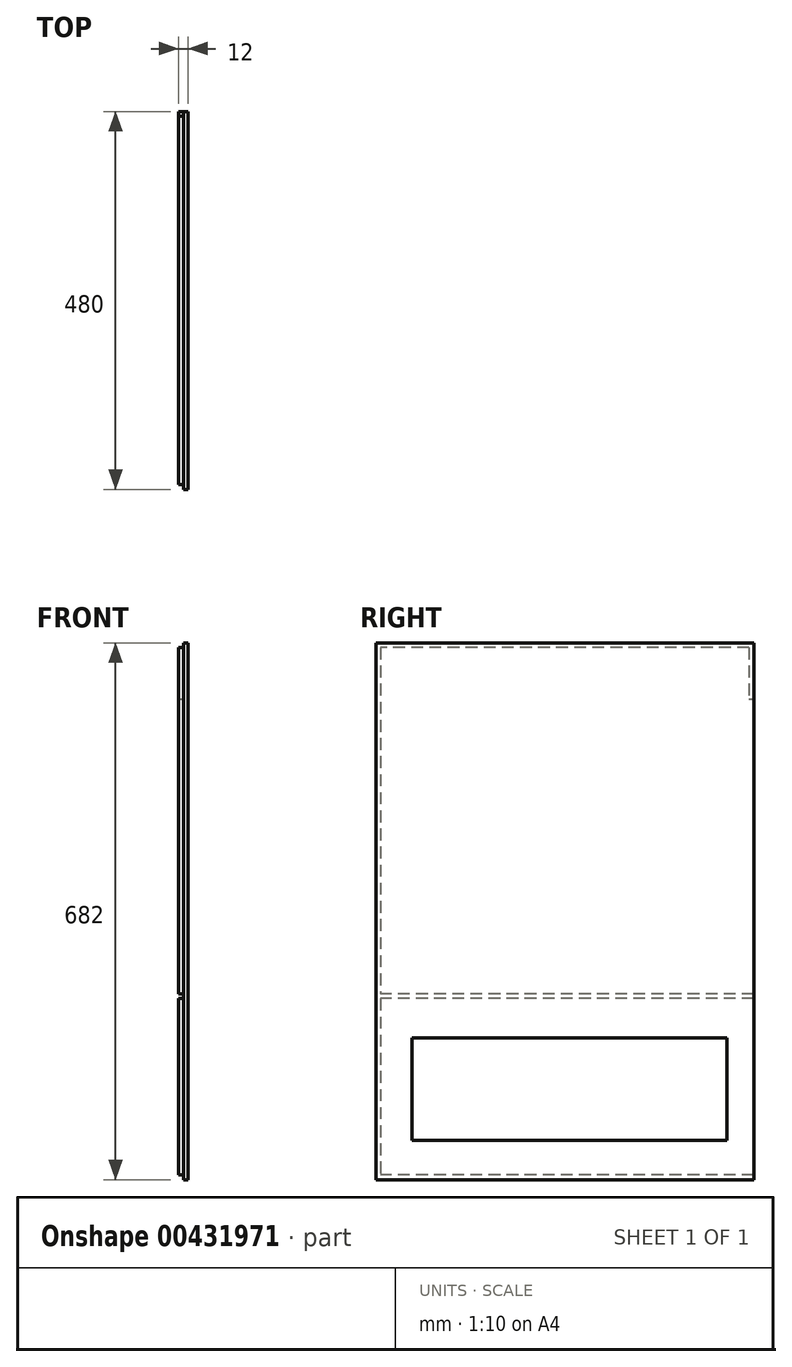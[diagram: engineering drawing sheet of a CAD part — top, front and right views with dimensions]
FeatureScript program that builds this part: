
annotation { "Feature Type Name" : "Feature", "Feature Type Description" : "" }
export const myFeature = defineFeature(function(context is Context, id is Id, definition is map)
    precondition{}
    {
        {
            var Q0;
            Q0=qCreatedBy(makeId("Right.planeOp"),FACE);
            var sketch = newSketch(context, id + "F0", { "sketchPlane" : qUnion([Q0])});
            skLineSegment(sketch, "E0.bottom", {"start": v(-240, 341) * mm, "end": v(240, 341) * mm});
            skLineSegment(sketch, "E0.top", {"start": v(-240, -341) * mm, "end": v(240, -341) * mm});
            skLineSegment(sketch, "E0.left", {"start": v(-240, 341) * mm, "end": v(-240, -341) * mm});
            skLineSegment(sketch, "E0.right", {"start": v(240, 341) * mm, "end": v(240, -341) * mm});
            skPoint(sketch, "E0.middle", {"position": v(0, 0) * mm});
            skSolve(sketch);
        }
        {
            var Q0;
            Q0=makeQuery(id+"F0.imprint","IMPRINT",FACE,{"disambiguationData":[TD([[makeQuery(id+"F0.imprint","IMPRINT",EDGE,{"derivedFrom":sQuery(id+"F0.wireOp",EDGE,"E0.bottom")}),-1.0]])]});
            extrude(context, id + "F1", {"entities" : qUnion([Q0]), "depth" : 12 * mm, "offsetDistance" : 25 * mm});
        }
        {
            var Q0;
            Q0=makeQuery(id+"F1.opExtrude","CAP_FACE",FACE,{"disambiguationData":[OSD([sQuery(id+"F0.wireOp",EDGE,"E0.bottom"),sQuery(id+"F0.wireOp",EDGE,"E0.top"),sQuery(id+"F0.wireOp",EDGE,"E0.left"),sQuery(id+"F0.wireOp",EDGE,"E0.right")])],"isStart":true});
            var sketch = newSketch(context, id + "F2", { "sketchPlane" : qUnion([Q0])});
            skLineSegment(sketch, "E1.bottom", {"start": v(240, 341) * mm, "end": v(234, 341) * mm});
            skLineSegment(sketch, "E1.top", {"start": v(240, -341) * mm, "end": v(234, -341) * mm});
            skLineSegment(sketch, "E1.left", {"start": v(240, 341) * mm, "end": v(240, -341) * mm});
            skLineSegment(sketch, "E1.right", {"start": v(234, 341) * mm, "end": v(234, -341) * mm});
            skSolve(sketch);
        }
        {
            var Q0;
            Q0=qSketchRegion(id+"F2",true);
            extrude(context, id + "F3", {"entities" : qUnion([Q0]), "operationType" : NewBodyOperationType.REMOVE, "oppositeDirection" : true, "depth" : 6 * mm, "offsetDistance" : 25 * mm});
        }
        {
            var Q0;
            {var subQ0=sQuery(id+"F0.wireOp",EDGE,"E0.bottom");var subQ1=sQuery(id+"F0.wireOp",EDGE,"E0.right");var subQ2=sQuery(id+"F0.wireOp",EDGE,"E0.top");Q0=makeQuery(id+"F3.boolean.opBoolean","SPLIT",FACE,{"disambiguationData":[TD([makeQuery(id+"F1.opExtrude","SWEPT_FACE",FACE,{"disambiguationData":[OSD([subQ1])]})])],"derivedFrom":makeQuery(id+"F1.opExtrude","CAP_FACE",FACE,{"disambiguationData":[OSD([subQ0,subQ2,sQuery(id+"F0.wireOp",EDGE,"E0.left"),subQ1])],"isStart":true})});}
            var sketch = newSketch(context, id + "F4", { "sketchPlane" : qUnion([Q0])});
            skLineSegment(sketch, "E2.bottom", {"start": v(-240, 341) * mm, "end": v(234, 341) * mm});
            skLineSegment(sketch, "E2.top", {"start": v(-240, 335) * mm, "end": v(234, 335) * mm});
            skLineSegment(sketch, "E2.left", {"start": v(-240, 341) * mm, "end": v(-240, 335) * mm});
            skLineSegment(sketch, "E2.right", {"start": v(234, 341) * mm, "end": v(234, 335) * mm});
            skSolve(sketch);
        }
        {
            var Q0;
            Q0=qSketchRegion(id+"F4",true);
            extrude(context, id + "F5", {"entities" : qUnion([Q0]), "operationType" : NewBodyOperationType.REMOVE, "oppositeDirection" : true, "depth" : 6 * mm, "offsetDistance" : 25 * mm});
        }
        {
            var Q0;
            {var subQ0=sQuery(id+"F0.wireOp",EDGE,"E0.bottom");var subQ1=sQuery(id+"F0.wireOp",EDGE,"E0.right");var subQ2=sQuery(id+"F0.wireOp",EDGE,"E0.top");Q0=makeQuery(id+"F3.boolean.opBoolean","SPLIT",FACE,{"disambiguationData":[TD([makeQuery(id+"F1.opExtrude","SWEPT_FACE",FACE,{"disambiguationData":[OSD([subQ1])]})])],"derivedFrom":makeQuery(id+"F1.opExtrude","CAP_FACE",FACE,{"disambiguationData":[OSD([subQ0,subQ2,sQuery(id+"F0.wireOp",EDGE,"E0.left"),subQ1])],"isStart":true})});}
            var sketch = newSketch(context, id + "F6", { "sketchPlane" : qUnion([Q0])});
            skLineSegment(sketch, "E3.bottom", {"start": v(-240, 335) * mm, "end": v(-234, 335) * mm});
            skLineSegment(sketch, "E3.top", {"start": v(-240, 269) * mm, "end": v(-234, 269) * mm});
            skLineSegment(sketch, "E3.left", {"start": v(-240, 335) * mm, "end": v(-240, 269) * mm});
            skLineSegment(sketch, "E3.right", {"start": v(-234, 335) * mm, "end": v(-234, 269) * mm});
            skSolve(sketch);
        }
        {
            var Q0;
            Q0=qSketchRegion(id+"F6",true);
            extrude(context, id + "F7", {"entities" : qUnion([Q0]), "operationType" : NewBodyOperationType.REMOVE, "oppositeDirection" : true, "depth" : 6 * mm, "offsetDistance" : 25 * mm});
        }
        {
            var Q0;
            {var subQ0=sQuery(id+"F0.wireOp",EDGE,"E0.bottom");var subQ1=sQuery(id+"F0.wireOp",EDGE,"E0.right");var subQ2=sQuery(id+"F0.wireOp",EDGE,"E0.top");Q0=makeQuery(id+"F3.boolean.opBoolean","SPLIT",FACE,{"disambiguationData":[TD([makeQuery(id+"F1.opExtrude","SWEPT_FACE",FACE,{"disambiguationData":[OSD([subQ1])]})])],"derivedFrom":makeQuery(id+"F1.opExtrude","CAP_FACE",FACE,{"disambiguationData":[OSD([subQ0,subQ2,sQuery(id+"F0.wireOp",EDGE,"E0.left"),subQ1])],"isStart":true})});}
            var sketch = newSketch(context, id + "F8", { "sketchPlane" : qUnion([Q0])});
            skLineSegment(sketch, "E4.bottom", {"start": v(-240, -111) * mm, "end": v(234, -111) * mm});
            skLineSegment(sketch, "E4.top", {"start": v(-240, -105) * mm, "end": v(234, -105) * mm});
            skLineSegment(sketch, "E4.left", {"start": v(-240, -111) * mm, "end": v(-240, -105) * mm});
            skLineSegment(sketch, "E4.right", {"start": v(234, -111) * mm, "end": v(234, -105) * mm});
            skSolve(sketch);
        }
        {
            var Q0;
            Q0=qSketchRegion(id+"F8",true);
            extrude(context, id + "F9", {"entities" : qUnion([Q0]), "operationType" : NewBodyOperationType.REMOVE, "oppositeDirection" : true, "depth" : 6 * mm, "offsetDistance" : 25 * mm});
        }
        {
            var Q0;
            Q0=makeQuery(id+"F1.opExtrude","CAP_FACE",FACE,{"disambiguationData":[OSD([sQuery(id+"F0.wireOp",EDGE,"E0.bottom"),sQuery(id+"F0.wireOp",EDGE,"E0.top"),sQuery(id+"F0.wireOp",EDGE,"E0.left"),sQuery(id+"F0.wireOp",EDGE,"E0.right")])],"isStart":false});
            var sketch = newSketch(context, id + "F10", { "sketchPlane" : qUnion([Q0])});
            skLineSegment(sketch, "E5.bottom", {"start": v(-194, -291) * mm, "end": v(206, -291) * mm});
            skLineSegment(sketch, "E5.top", {"start": v(-194, -161) * mm, "end": v(206, -161) * mm});
            skLineSegment(sketch, "E5.left", {"start": v(-194, -291) * mm, "end": v(-194, -161) * mm});
            skLineSegment(sketch, "E5.right", {"start": v(206, -291) * mm, "end": v(206, -161) * mm});
            skSolve(sketch);
        }
        {
            var Q0;
            Q0=qSketchRegion(id+"F10",true);
            extrude(context, id + "F11", {"entities" : qUnion([Q0]), "operationType" : NewBodyOperationType.REMOVE, "endBound" : BoundingType.UP_TO_NEXT, "oppositeDirection" : true, "depth" : 25 * mm});
        }
        {
            var Q0;
            {var subQ0=sQuery(id+"F0.wireOp",EDGE,"E0.top");var subQ1=makeQuery(id+"F1.opExtrude","SWEPT_FACE",FACE,{"disambiguationData":[OSD([subQ0])]});var subQ2=sQuery(id+"F0.wireOp",EDGE,"E0.right");var subQ3=makeQuery(id+"F1.opExtrude","SWEPT_FACE",FACE,{"disambiguationData":[OSD([subQ2])]});var subQ5=sQuery(id+"F0.wireOp",EDGE,"E0.bottom");Q0=makeQuery(id+"F9.boolean.opBoolean","SPLIT",FACE,{"disambiguationData":[TD([subQ1])],"derivedFrom":makeQuery(id+"F3.boolean.opBoolean","SPLIT",FACE,{"disambiguationData":[TD([subQ3])],"derivedFrom":makeQuery(id+"F1.opExtrude","CAP_FACE",FACE,{"disambiguationData":[OSD([subQ5,subQ0,sQuery(id+"F0.wireOp",EDGE,"E0.left"),subQ2])],"isStart":true})})});}
            var sketch = newSketch(context, id + "F12", { "sketchPlane" : qUnion([Q0])});
            skLineSegment(sketch, "E6.bottom", {"start": v(-240, -341) * mm, "end": v(234, -341) * mm});
            skLineSegment(sketch, "E6.top", {"start": v(-240, -335) * mm, "end": v(234, -335) * mm});
            skLineSegment(sketch, "E6.left", {"start": v(-240, -341) * mm, "end": v(-240, -335) * mm});
            skLineSegment(sketch, "E6.right", {"start": v(234, -341) * mm, "end": v(234, -335) * mm});
            skSolve(sketch);
        }
        {
            var Q0;
            Q0=qSketchRegion(id+"F12",true);
            extrude(context, id + "F13", {"entities" : qUnion([Q0]), "operationType" : NewBodyOperationType.REMOVE, "oppositeDirection" : true, "depth" : 6 * mm, "offsetDistance" : 25 * mm});
        }
    });
